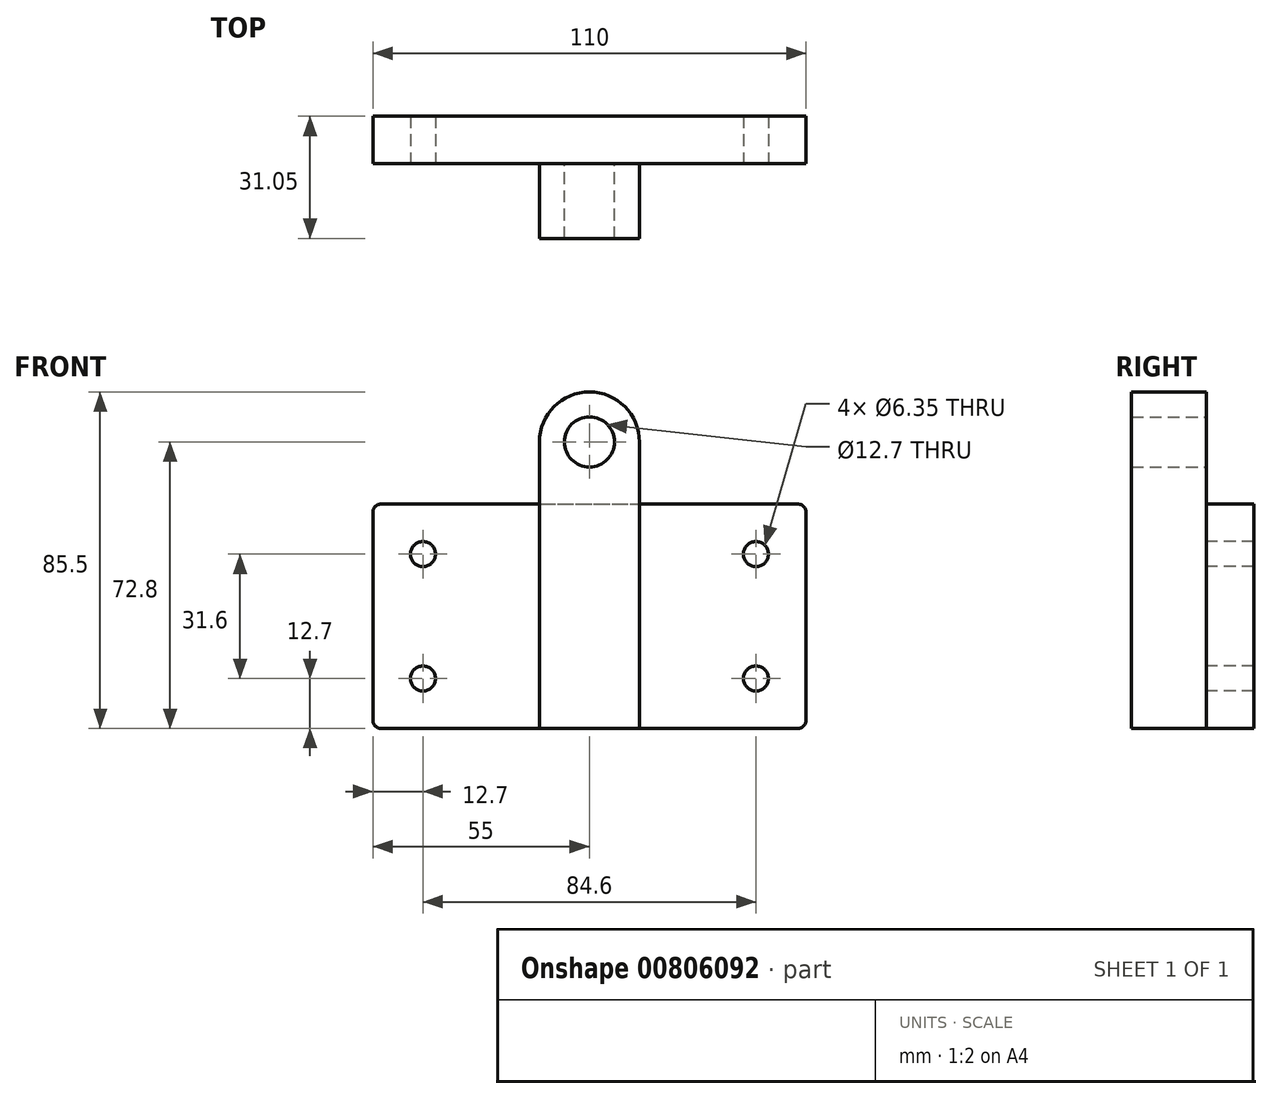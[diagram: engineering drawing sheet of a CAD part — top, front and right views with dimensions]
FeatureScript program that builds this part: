
annotation { "Feature Type Name" : "Feature", "Feature Type Description" : "" }
export const myFeature = defineFeature(function(context is Context, id is Id, definition is map)
    precondition{}
    {
        {
            var Q0;
            Q0=qCreatedBy(makeId("Front.planeOp"),FACE);
            var sketch = newSketch(context, id + "F0", { "sketchPlane" : qUnion([Q0])});
            skLineSegment(sketch, "E0.bottom", {"start": v(-53, 28.5) * mm, "end": v(53, 28.5) * mm});
            skLineSegment(sketch, "E0.top", {"start": v(-53, -28.5) * mm, "end": v(53, -28.5) * mm});
            skLineSegment(sketch, "E0.left", {"start": v(-55, 26.5) * mm, "end": v(-55, -26.5) * mm});
            skLineSegment(sketch, "E0.right", {"start": v(55, 26.5) * mm, "end": v(55, -26.5) * mm});
            skPoint(sketch, "E0.middle", {"position": v(0, 0) * mm});
            skPoint(sketch, "E1.visualSharp", {"position": v(-55, 28.5) * mm});
            skArc(sketch, "E1.filletArc", {"start": v(-53, 28.5) * mm, "mid": v(-54.41, 27.91) * mm, "end": v(-55, 26.5) * mm});
            skPoint(sketch, "E2.visualSharp", {"position": v(-55, -28.5) * mm});
            skArc(sketch, "E2.filletArc", {"start": v(-55, -26.5) * mm, "mid": v(-54.41, -27.91) * mm, "end": v(-53, -28.5) * mm});
            skPoint(sketch, "E3.visualSharp", {"position": v(55, 28.5) * mm});
            skArc(sketch, "E3.filletArc", {"start": v(55, 26.5) * mm, "mid": v(54.41, 27.91) * mm, "end": v(53, 28.5) * mm});
            skPoint(sketch, "E4.visualSharp", {"position": v(55, -28.5) * mm});
            skArc(sketch, "E4.filletArc", {"start": v(53, -28.5) * mm, "mid": v(54.41, -27.91) * mm, "end": v(55, -26.5) * mm});
            skLineSegment(sketch, "E5.bottom", {"start": v(-12.7, 57) * mm, "end": v(12.7, 57) * mm});
            skLineSegment(sketch, "E5.top", {"start": v(-12.7, -28.5) * mm, "end": v(12.7, -28.5) * mm});
            skLineSegment(sketch, "E5.left", {"start": v(-12.7, 57) * mm, "end": v(-12.7, -28.5) * mm});
            skLineSegment(sketch, "E5.right", {"start": v(12.7, 57) * mm, "end": v(12.7, -28.5) * mm});
            skLineSegment(sketch, "E6", {"start": v(0, 0) * mm, "end": v(0, -28.5) * mm, "construction": true});
            skCircle(sketch, "E7", {"center": v(0, 44.3) * mm, "radius": 12.7 * mm});
            skCircle(sketch, "E8", {"center": v(0, 44.3) * mm, "radius": 6.35 * mm});
            skCircle(sketch, "E9", {"center": v(-42.3, 15.8) * mm, "radius": 3.18 * mm});
            skCircle(sketch, "E10", {"center": v(-42.3, -15.8) * mm, "radius": 3.18 * mm});
            skCircle(sketch, "E11.MirrorC", {"center": v(42.3, -15.8) * mm, "radius": 3.18 * mm});
            skCircle(sketch, "E12.MirrorC", {"center": v(42.3, 15.8) * mm, "radius": 3.18 * mm});
            skSolve(sketch);
        }
        {
            var Q0;
            {var subQ0=sQuery(id+"F0.wireOp",EDGE,"E5.right");var subQ1=sQuery(id+"F0.wireOp",EDGE,"E0.bottom");var subQ2=makeQuery(id+"F0.imprint","INTERSECT",VERTEX,{"derivedFrom":[subQ1,subQ0]});Q0=makeQuery(id+"F0.imprint","IMPRINT",FACE,{"disambiguationData":[TD([[makeQuery(id+"F0.imprint","IMPRINT",EDGE,{"disambiguationData":[TD([[subQ2,1.0]])],"derivedFrom":subQ1}),-1.0]])]});}
            var Q1;
            Q1=makeQuery(id+"F0.imprint","IMPRINT",FACE,{"disambiguationData":[TD([[makeQuery(id+"F0.imprint","IMPRINT",EDGE,{"derivedFrom":sQuery(id+"F0.wireOp",EDGE,"E0.left")}),1.0]])]});
            var Q2;
            Q2=makeQuery(id+"F0.imprint","IMPRINT",FACE,{"disambiguationData":[TD([[makeQuery(id+"F0.imprint","IMPRINT",EDGE,{"derivedFrom":sQuery(id+"F0.wireOp",EDGE,"E0.right")}),-1.0]])]});
            extrude(context, id + "F1", {"entities" : qUnion([Q0, Q1, Q2]), "oppositeDirection" : true, "depth" : 12 * mm, "offsetDistance" : 25.4 * mm});
        }
        {
            var Q0;
            {var subQ0=sQuery(id+"F0.wireOp",EDGE,"E5.right");var subQ1=sQuery(id+"F0.wireOp",EDGE,"E0.bottom");var subQ2=makeQuery(id+"F0.imprint","INTERSECT",VERTEX,{"derivedFrom":[subQ1,subQ0]});Q0=makeQuery(id+"F0.imprint","IMPRINT",FACE,{"disambiguationData":[TD([[makeQuery(id+"F0.imprint","IMPRINT",EDGE,{"disambiguationData":[TD([[subQ2,1.0]])],"derivedFrom":subQ1}),-1.0]])]});}
            var Q1;
            {var subQ0=sQuery(id+"F0.wireOp",EDGE,"E5.right");var subQ1=sQuery(id+"F0.wireOp",EDGE,"E0.bottom");var subQ2=makeQuery(id+"F0.imprint","INTERSECT",VERTEX,{"derivedFrom":[subQ1,subQ0]});Q1=makeQuery(id+"F0.imprint","IMPRINT",FACE,{"disambiguationData":[TD([[makeQuery(id+"F0.imprint","IMPRINT",EDGE,{"disambiguationData":[TD([[subQ2,1.0]])],"derivedFrom":subQ1}),1.0]])]});}
            var Q2;
            Q2=makeQuery(id+"F0.imprint","IMPRINT",FACE,{"disambiguationData":[TD([[makeQuery(id+"F0.imprint","IMPRINT",EDGE,{"derivedFrom":sQuery(id+"F0.wireOp",EDGE,"E8")}),-1.0]])]});
            extrude(context, id + "F2", {"entities" : qUnion([Q0, Q1, Q2]), "operationType" : NewBodyOperationType.ADD, "depth" : 19.05 * mm, "offsetDistance" : 25.4 * mm});
        }
    });
